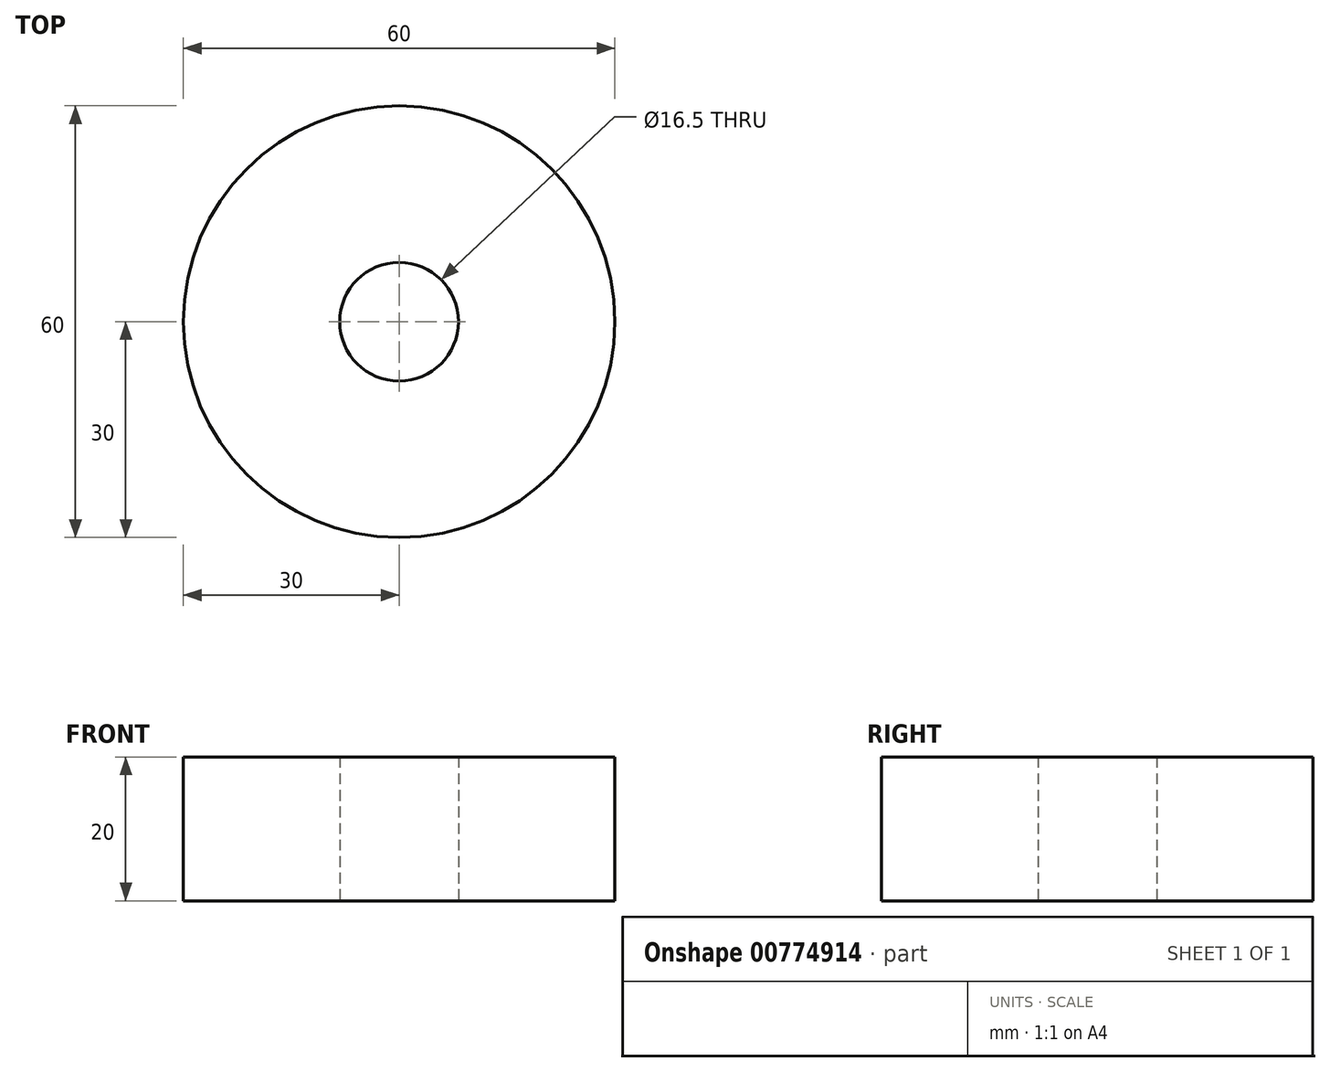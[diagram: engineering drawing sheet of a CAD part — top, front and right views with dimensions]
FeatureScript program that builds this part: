
annotation { "Feature Type Name" : "Feature", "Feature Type Description" : "" }
export const myFeature = defineFeature(function(context is Context, id is Id, definition is map)
    precondition{}
    {
        {
            var Q0;
            Q0=qCreatedBy(makeId("Top.planeOp"),FACE);
            var sketch = newSketch(context, id + "F0", { "sketchPlane" : qUnion([Q0])});
            skCircle(sketch, "E0", {"center": v(0, 0) * mm, "radius": 30 * mm});
            skCircle(sketch, "E1", {"center": v(0, 0) * mm, "radius": 8.25 * mm});
            skSolve(sketch);
        }
        {
            var Q0;
            Q0=makeQuery(id+"F0.imprint","IMPRINT",FACE,{"disambiguationData":[TD([[makeQuery(id+"F0.imprint","IMPRINT",EDGE,{"derivedFrom":sQuery(id+"F0.wireOp",EDGE,"E0")}),1.0]])]});
            extrude(context, id + "F1", {"entities" : qUnion([Q0]), "depth" : 20 * mm, "offsetDistance" : 25 * mm});
        }
    });
